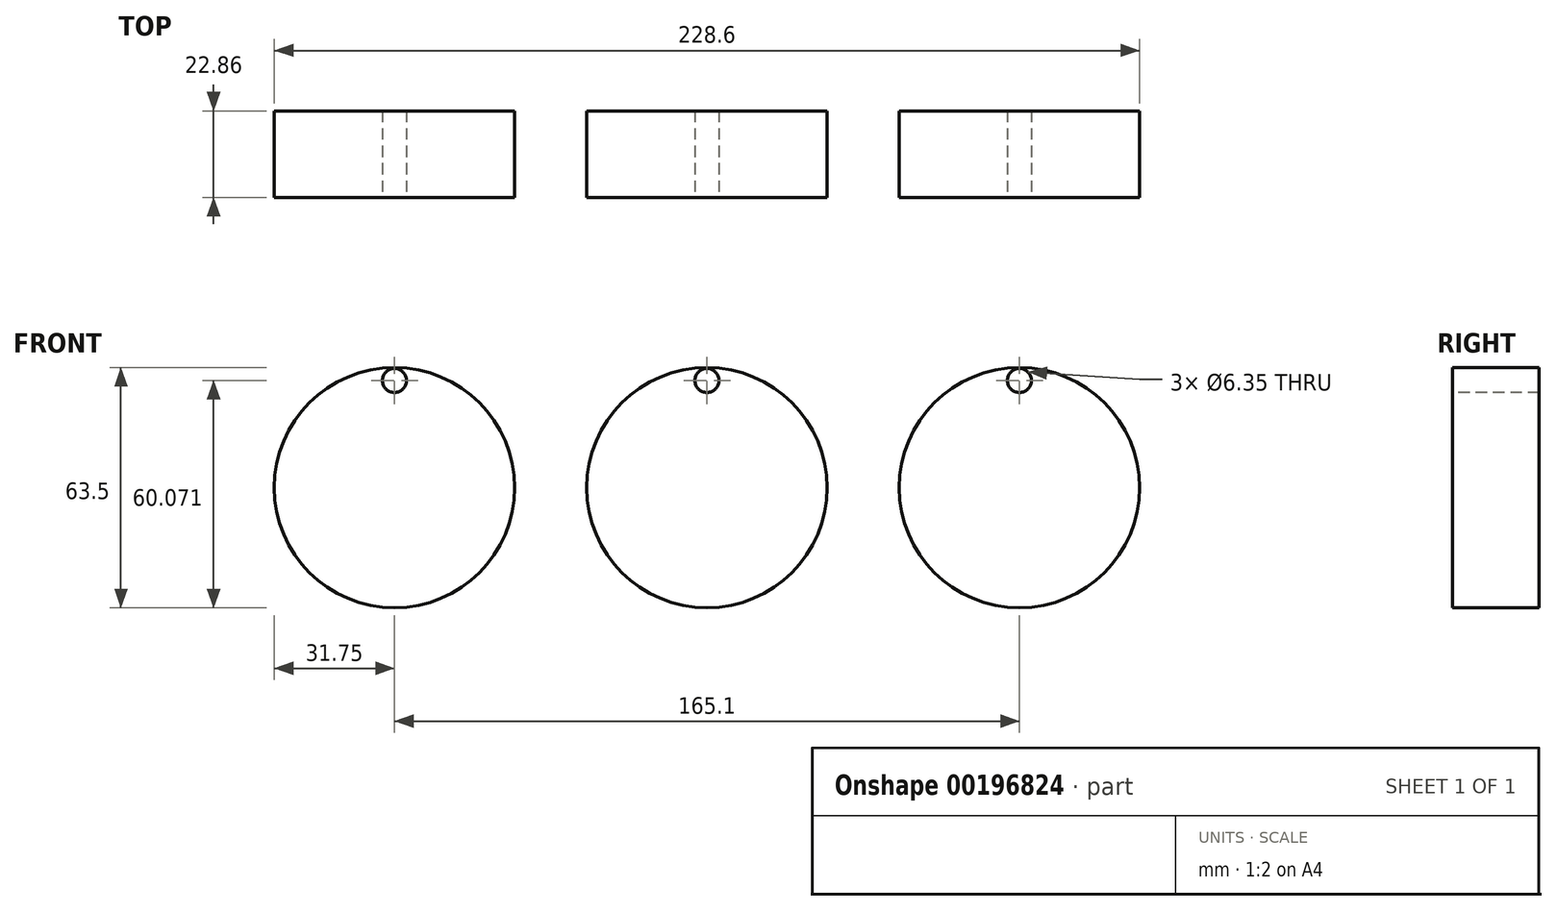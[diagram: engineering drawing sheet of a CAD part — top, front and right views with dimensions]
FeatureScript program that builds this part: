
annotation { "Feature Type Name" : "Feature", "Feature Type Description" : "" }
export const myFeature = defineFeature(function(context is Context, id is Id, definition is map)
    precondition{}
    {
        {
            var Q0;
            Q0=qCreatedBy(makeId("Front.planeOp"),FACE);
            var sketch = newSketch(context, id + "F0", { "sketchPlane" : qUnion([Q0])});
            skCircle(sketch, "E0", {"center": v(0, 0) * mm, "radius": 38.1 * mm});
            skCircle(sketch, "E1", {"center": v(82.55, 0) * mm, "radius": 38.1 * mm});
            skCircle(sketch, "E2", {"center": v(-82.55, 0) * mm, "radius": 38.1 * mm});
            skCircle(sketch, "E3", {"center": v(-82.55, 0) * mm, "radius": 31.75 * mm});
            skCircle(sketch, "E4", {"center": v(0, 0) * mm, "radius": 31.75 * mm});
            skCircle(sketch, "E5", {"center": v(82.55, 0) * mm, "radius": 31.75 * mm});
            skLineSegment(sketch, "E6.bottom", {"start": v(-133.35, 50.8) * mm, "end": v(133.35, 50.8) * mm});
            skLineSegment(sketch, "E6.top", {"start": v(-133.35, -50.8) * mm, "end": v(133.35, -50.8) * mm});
            skLineSegment(sketch, "E6.left", {"start": v(-133.35, 50.8) * mm, "end": v(-133.35, -50.8) * mm});
            skLineSegment(sketch, "E6.right", {"start": v(133.35, 50.8) * mm, "end": v(133.35, -50.8) * mm});
            skSolve(sketch);
        }
        {
            var Q0;
            Q0=makeQuery(id+"F0.imprint","IMPRINT",FACE,{"disambiguationData":[TD([[makeQuery(id+"F0.imprint","IMPRINT",EDGE,{"derivedFrom":sQuery(id+"F0.wireOp",EDGE,"E3")}),1.0]])]});
            var Q1;
            Q1=makeQuery(id+"F0.imprint","IMPRINT",FACE,{"disambiguationData":[TD([[makeQuery(id+"F0.imprint","IMPRINT",EDGE,{"derivedFrom":sQuery(id+"F0.wireOp",EDGE,"E4")}),1.0]])]});
            var Q2;
            Q2=makeQuery(id+"F0.imprint","IMPRINT",FACE,{"disambiguationData":[TD([[makeQuery(id+"F0.imprint","IMPRINT",EDGE,{"derivedFrom":sQuery(id+"F0.wireOp",EDGE,"E5")}),1.0]])]});
            extrude(context, id + "F1", {"entities" : qUnion([Q0, Q1, Q2]), "depth" : 22.86 * mm, "offsetDistance" : 25.4 * mm});
        }
        {
            var Q0;
            Q0=makeQuery(id+"F1.opExtrude","CAP_FACE",FACE,{"disambiguationData":[OSD([sQuery(id+"F0.wireOp",EDGE,"E4")])],"isStart":false});
            var sketch = newSketch(context, id + "F2", { "sketchPlane" : qUnion([Q0])});
            skCircle(sketch, "E7", {"center": v(0, 28.32) * mm, "radius": 3.18 * mm});
            skCircle(sketch, "E8", {"center": v(-82.55, 28.32) * mm, "radius": 3.18 * mm});
            skCircle(sketch, "E9", {"center": v(82.55, 28.32) * mm, "radius": 3.18 * mm});
            skSolve(sketch);
        }
        {
            var Q0;
            Q0=makeQuery(id+"F2.imprint","IMPRINT",FACE,{"disambiguationData":[TD([[makeQuery(id+"F2.imprint","IMPRINT",EDGE,{"derivedFrom":sQuery(id+"F2.wireOp",EDGE,"E8")}),1.0]])]});
            extrude(context, id + "F3", {"entities" : qUnion([Q0]), "operationType" : NewBodyOperationType.REMOVE, "oppositeDirection" : true, "depth" : 25.4 * mm, "offsetDistance" : 25.4 * mm});
        }
        {
            var Q0;
            Q0=makeQuery(id+"F2.imprint","IMPRINT",FACE,{"disambiguationData":[TD([[makeQuery(id+"F2.imprint","IMPRINT",EDGE,{"derivedFrom":sQuery(id+"F2.wireOp",EDGE,"E7")}),1.0]])]});
            var Q1;
            Q1=sQuery(id+"F2.wireOp",EDGE,"E7");
            extrude(context, id + "F4", {"entities" : qUnion([Q0]), "operationType" : NewBodyOperationType.REMOVE, "surfaceEntities" : qUnion([Q1]), "oppositeDirection" : true, "depth" : 25.4 * mm, "offsetDistance" : 25.4 * mm});
        }
        {
            var Q0;
            Q0=makeQuery(id+"F2.imprint","IMPRINT",FACE,{"disambiguationData":[TD([[makeQuery(id+"F2.imprint","IMPRINT",EDGE,{"derivedFrom":sQuery(id+"F2.wireOp",EDGE,"E9")}),1.0]])]});
            var Q1;
            Q1=sQuery(id+"F2.wireOp",EDGE,"E9");
            extrude(context, id + "F5", {"entities" : qUnion([Q0]), "operationType" : NewBodyOperationType.REMOVE, "surfaceEntities" : qUnion([Q1]), "oppositeDirection" : true, "depth" : 25.4 * mm, "offsetDistance" : 25.4 * mm});
        }
    });
